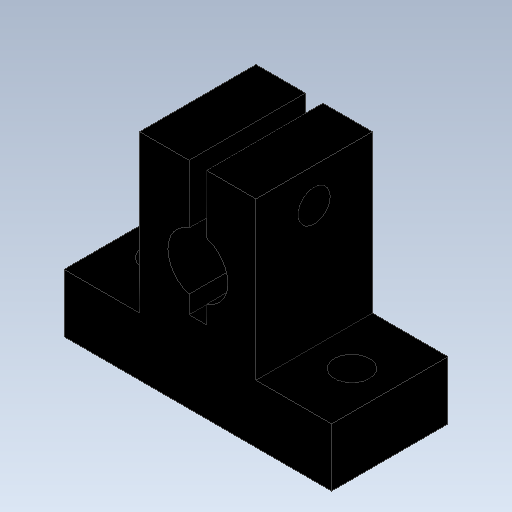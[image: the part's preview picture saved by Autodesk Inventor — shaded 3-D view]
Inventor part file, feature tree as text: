
AUTODESK INVENTOR PART (.ipt)
format: ipt  version: 2020 (Build 240168000, 168)  size: 151,040 bytes
history: native  units: mm
features: sketch x3, extrude x2, hole x1
ambient origin geometry x8: Origin, YZ Plane, XZ Plane, XY Plane, X Axis, Y Axis, Z Axis, Center Point
bodies: Solid1 (feature_tree)
feature tree (6):
  extrude  "Extrusion1"  Depth=20.0mm
  hole  "Hole1"  [1 undecoded]
  extrude  "Extrusion2"  Depth=3.0mm
  sketch  "Sketch1"  dims[d0=10.0mm d1=20.0mm]
  sketch  "Sketch2"  dims[d2=10.3mm d3=12.0mm]
  sketch  "Sketch3"  dims[d4=15.0mm d5=3.0mm d6=8.0mm d7=13.0mm d8=20.0mm d9=0.0mm d10=6.0mm d11=6.0mm d12=4.0mm d13=2.0mm d14=90.0deg d15=8.0mm d16=20.594885mm d17=6.0mm d18=5.5mm d19=8.0mm d21=8.0mm d22=13.0mm d23=0.0mm]
note: 1 required parameter value undecoded (feature->parameter linkage not recoverable at this tier; creation-order binding heuristic only, values carry confidence <= 0.55)
